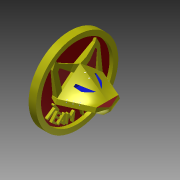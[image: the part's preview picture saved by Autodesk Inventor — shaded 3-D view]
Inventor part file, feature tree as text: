
AUTODESK INVENTOR PART (.ipt)
format: ipt  version: 2014 (Build 180170000, 170)  size: 811,008 bytes
history: native  units: in
note: dims shown in document units (in); Inventor stores cm internally (conversion verified against a paired STEP export)
features: sketch x20, extrude x13, plane x9, loft x4, projected_geometry x4, other x3, mirror x1, emboss x1
ambient origin geometry x8: Origin, YZ Plane, XZ Plane, XY Plane, X Axis, Y Axis, Z Axis, Center Point
bodies: Solid1 (feature_tree)
feature tree (55):
  sketch  "Sketch1"  dims[d0=0.7559in d1=0.7559in]
  plane  "Work Plane1"
  loft  "Loft1"
  extrude  "Extrusion1"  Depth=0.2in
  plane  "Work Plane4"
  loft  "Loft2"
  plane  "Work Plane5"
  loft  "Loft3"
  loft  "Loft4"
  extrude  "Extrusion2"  TaperAngle=0.0deg  [1 undecoded]
  plane  "Work Plane6"
  extrude  "Extrusion3"  Depth=1.0in
  extrude  "Extrusion4"  Depth=1.0651in
  extrude  "Extrusion5"  Depth=0.962in
  plane  "Work Plane7"
  extrude  "Extrusion6"  Depth=0.075in
  plane  "Work Plane8"
  other  "Work Axis1"
  plane  "Work Plane9"
  extrude  "Extrusion7"  Depth=0.06in
  mirror  "Mirror3"
  extrude  "Extrusion8"  Depth=0.05in
  plane  "Work Plane10"
  extrude  "Extrusion9"  Depth=0.0625in
  plane  "Work Plane11"
  extrude  "Extrusion10"  Depth=0.075in
  extrude  "Extrusion11"  TaperAngle=0.0deg  [1 undecoded]
  extrude  "Extrusion12"  Depth=0.2in
  extrude  "Extrusion13"  TaperAngle=0.0deg  [1 undecoded]
  emboss  "Emboss1"
  sketch  "Sketch2"  dims[d2=0.9963in d3=0.2in]
  sketch  "Sketch3"  dims[d4=0.5in d6=0.08in]
  sketch  "Sketch4"  dims[d7=0.55in d8=150.0deg]
  other  "Edges1"
  sketch  "Sketch5"  dims[d9=150.0deg d14=0.33in]
  projected_geometry  "Projected Loop1"
  other  "Edges2"
  sketch  "Sketch6"  dims[d15=0.66in d18=0.0in d19=90.0deg]
  sketch  "Sketch7"  dims[d20=0.0in d21=90.0deg d22=1.0in]
  sketch  "Sketch8"  dims[d26=1.0651in d28=1.0651in]
  sketch  "Sketch9"  dims[d29=0.0in d30=0.962in]
  sketch  "Sketch10"  dims[d31=0.962in d32=0.075in]
  sketch  "Sketch11"  dims[d33=0.15in d34=0.06in]
  sketch  "Sketch12"  dims[d35=0.1in d36=0.05in]
  sketch  "Sketch13"  dims[d37=0.45in d38=0.0in d39=0.0625in]
  projected_geometry  "Projected Loop2"
  projected_geometry  "Projected Loop3"
  sketch  "Sketch14"  dims[d40=0.01in d41=0.075in]
  projected_geometry  "Projected Loop4"
  sketch  "Sketch15"  dims[d42=0.01in d43=0.0in d44=90.0deg]
  sketch  "Sketch16"  dims[d45=0.0in d46=90.0deg d47=0.2in]
  sketch  "Sketch17"  dims[d48=0.07in d49=0.0in d50=90.0deg]
  sketch  "Sketch18"  dims[d51=0.0in d52=90.0deg]
  sketch  "Sketch19"  dims[d53=0.01in]
  sketch  "Sketch20"  dims[d54=0.01in d55=0.0344in d56=150.0deg d57=60.0deg d58=150.0deg d59=0.7in d60=0.05in d61=0.05in d62=0.05in d63=0.05in d64=0.05in d65=0.01in d66=0.0in d67=90.0deg d68=0.0in d69=90.0deg d70=0.1in d71=0.4in d72=0.15in d73=0.05in d74=0.0in d75=0.02in d77=0.15in d78=0.02in d79=0.1in d80=0.1in d81=0.1in d82=0.02in d83=0.15in d84=0.05in d85=0.0in d86=0.045in d87=0.0in d88=0.025in d89=0.0in d90=0.02in d91=0.02in d92=0.005in d93=0.0in d94=90.0deg d95=0.4466in d96=1.0in d97=0.0in d98=1.0in d99=0.0in d100=0.6528in d101=0.0in d102=0.0in d103=1.0in d104=0.0in d106=90.0deg d107=1.0in d108=0.0in d109=1.65in d110=0.1in d111=0.075in d112=0.0in d113=0.1in d114=0.075in d115=0.0in d116=0.05in d117=0.0in]
note: 3 required parameter values undecoded (feature->parameter linkage not recoverable at this tier; creation-order binding heuristic only, values carry confidence <= 0.55)
